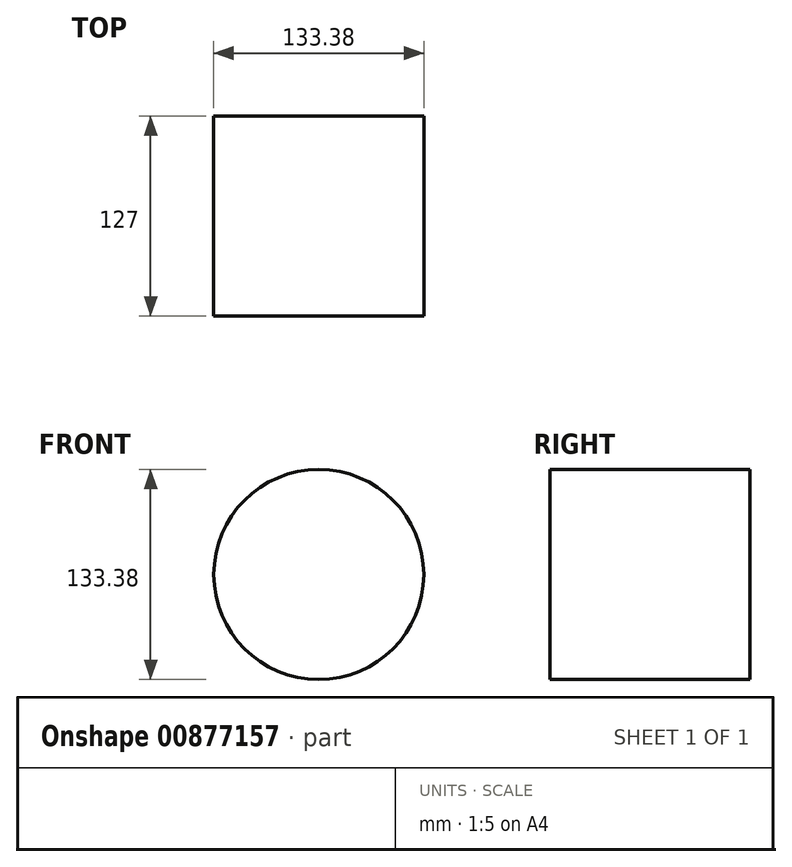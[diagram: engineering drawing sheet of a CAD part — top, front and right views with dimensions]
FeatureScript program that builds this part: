
annotation { "Feature Type Name" : "Feature", "Feature Type Description" : "" }
export const myFeature = defineFeature(function(context is Context, id is Id, definition is map)
    precondition{}
    {
        {
            var Q0;
            Q0=qCreatedBy(makeId("Front.planeOp"),FACE);
            var sketch = newSketch(context, id + "F0", { "sketchPlane" : qUnion([Q0])});
            skLineSegment(sketch, "E0.bottom", {"start": v(-63.5, 63.5) * mm, "end": v(63.5, 63.5) * mm});
            skLineSegment(sketch, "E0.top", {"start": v(-63.5, -63.5) * mm, "end": v(63.5, -63.5) * mm});
            skLineSegment(sketch, "E0.left", {"start": v(-63.5, 63.5) * mm, "end": v(-63.5, -63.5) * mm});
            skLineSegment(sketch, "E0.right", {"start": v(63.5, 63.5) * mm, "end": v(63.5, -63.5) * mm});
            skPoint(sketch, "E0.middle", {"position": v(0, 0) * mm});
            skSolve(sketch);
        }
        {
            var Q0;
            Q0=makeQuery(id+"F0.imprint","IMPRINT",FACE,{"disambiguationData":[TD([[makeQuery(id+"F0.imprint","IMPRINT",EDGE,{"derivedFrom":sQuery(id+"F0.wireOp",EDGE,"E0.bottom")}),-1.0]])]});
            var sketch = newSketch(context, id + "F1", { "sketchPlane" : qUnion([Q0])});
            skCircle(sketch, "E1", {"center": v(0, 0) * mm, "radius": 66.69 * mm});
            skSolve(sketch);
        }
        {
            var Q0;
            Q0=qSketchRegion(id+"F1",true);
            extrude(context, id + "F2", {"entities" : qUnion([Q0]), "depth" : 127 * mm, "offsetDistance" : 25.4 * mm});
        }
    });
